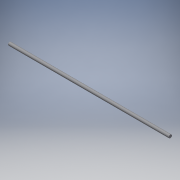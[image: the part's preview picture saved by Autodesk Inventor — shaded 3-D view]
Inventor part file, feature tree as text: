
AUTODESK INVENTOR PART (.ipt)
format: ipt  version: 2019 (Build 230136000, 136)  size: 90,624 bytes
history: native  units: mm
features: extrude x1, sketch x1
ambient origin geometry x8: Origin, YZ Plane, XZ Plane, XY Plane, X Axis, Y Axis, Z Axis, Center Point
bodies: Solid1 (feature_tree)
feature tree (2):
  extrude  "Extrusion1"  Depth=395.0mm TaperAngle=0.0deg
  sketch  "Sketch1"  dims[d0=8.0mm d1=395.0mm d2=0.0mm]
